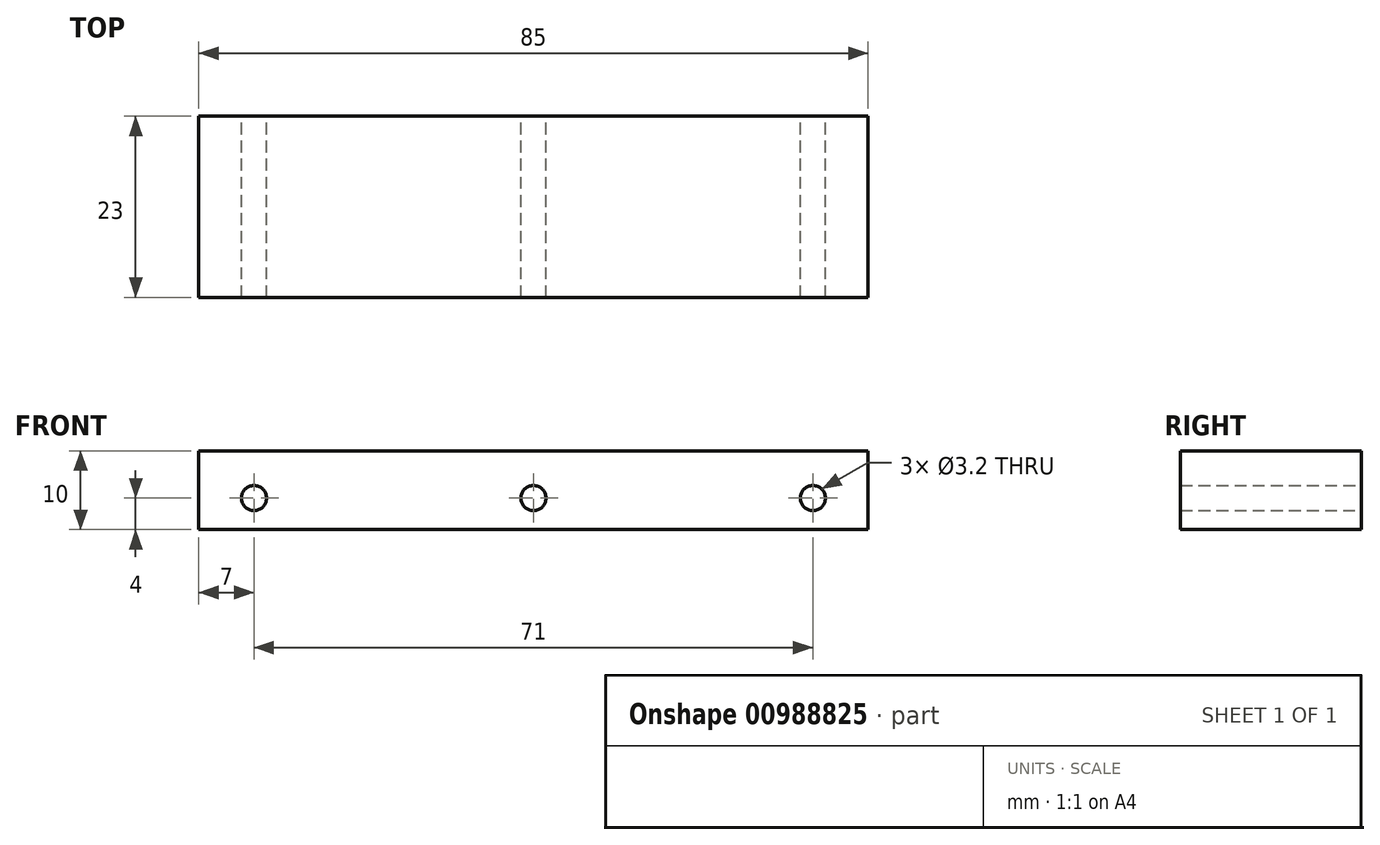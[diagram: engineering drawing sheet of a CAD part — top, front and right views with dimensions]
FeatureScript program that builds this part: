
annotation { "Feature Type Name" : "Feature", "Feature Type Description" : "" }
export const myFeature = defineFeature(function(context is Context, id is Id, definition is map)
    precondition{}
    {
        {
            var Q0;
            Q0=qCreatedBy(makeId("Front.planeOp"),FACE);
            var sketch = newSketch(context, id + "F0", { "sketchPlane" : qUnion([Q0])});
            skLineSegment(sketch, "E0.top", {"start": v(42.5, -4) * mm, "end": v(-42.5, -4) * mm});
            skLineSegment(sketch, "E0.left", {"start": v(42.5, 4) * mm, "end": v(42.5, -4) * mm});
            skLineSegment(sketch, "E0.right", {"start": v(-42.5, 4) * mm, "end": v(-42.5, -4) * mm});
            skPoint(sketch, "E0.middle", {"position": v(0, 0) * mm});
            skLineSegment(sketch, "E1.bottom", {"start": v(-42.5, 4) * mm, "end": v(42.5, 4) * mm, "construction": true});
            skLineSegment(sketch, "E1.top", {"start": v(-42.5, 6) * mm, "end": v(42.5, 6) * mm});
            skLineSegment(sketch, "E1.left", {"start": v(-42.5, 4) * mm, "end": v(-42.5, 6) * mm});
            skLineSegment(sketch, "E1.right", {"start": v(42.5, 4) * mm, "end": v(42.5, 6) * mm});
            skCircle(sketch, "E2", {"center": v(0, 0) * mm, "radius": 1.6 * mm});
            skCircle(sketch, "E3", {"center": v(35.5, 0) * mm, "radius": 1.6 * mm});
            skCircle(sketch, "E4", {"center": v(-35.5, 0) * mm, "radius": 1.6 * mm});
            skSolve(sketch);
        }
        {
            var Q0;
            Q0=makeQuery(id+"F0.imprint","IMPRINT",FACE,{"disambiguationData":[TD([[makeQuery(id+"F0.imprint","IMPRINT",EDGE,{"derivedFrom":sQuery(id+"F0.wireOp",EDGE,"E0.top")}),-1.0]])]});
            extrude(context, id + "F1", {"entities" : qUnion([Q0]), "endBound" : BoundingType.SYMMETRIC, "depth" : 23 * mm, "offsetDistance" : 25 * mm});
        }
    });
